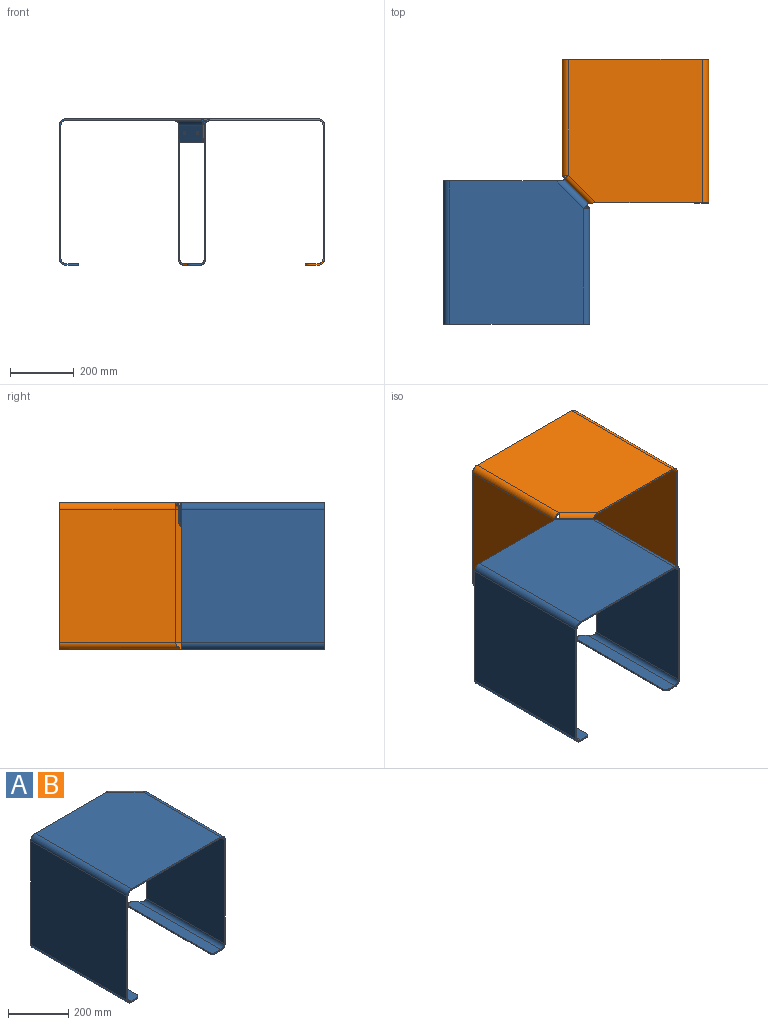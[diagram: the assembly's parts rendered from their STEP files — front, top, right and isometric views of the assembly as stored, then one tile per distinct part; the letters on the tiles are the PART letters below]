
ASSEMBLY  parts=2 mates=1
PART A: 56 faces, bbox 460x464.1x460 mm
  f0: plane 333.93x5mm, normal (0,1,0), area 1669.7mm2, adj f2,f3,f39,f52
  f1: plane 420x5mm, normal (0,-1,0), area 2100mm2, adj f2,f3,f21,f40
  f2: plane 450x420mm, normal (0,0,1), area 185296.3mm2, adj f0,f1,f22,f41,f54
  f3: plane 450x420mm, normal (0,0,-1), area 185296.3mm2, adj f0,f1,f23,f42,f55
  f4: plane 5x1.21mm, normal (0,0,1), area 6.1mm2, adj f6,f7,f8,f20
  f5: plane 420x5mm, normal (0,-1,0), area 2100mm2, adj f7,f8,f17,f21
  f6: plane 420x5mm, normal (0,1,0), area 2100mm2, adj f4,f7,f8,f16
  f7: plane 420x365.15mm, normal (1,0,0), area 153361.8mm2, adj f4,f5,f6,f18,f22
  f8: plane 420x365.15mm, normal (-1,0,0), area 153361.8mm2, adj f4,f5,f6,f19,f23
  f9: plane 25x5mm, normal (0,-1,0), area 125mm2, adj f12,f13,f14,f17
  f10: plane 373.93x5mm, normal (-1,0,0), area 1869.7mm2, adj f12,f13,f14,f15
  f11: plane 14.39x14.39mm, normal (0.71,0.71,0), area 101.8mm2, adj f12,f13,f15,f16
  f12: plane 403.93x40mm, normal (0,0,-1), area 15879.5mm2, adj f9,f10,f11,f14,f15,f18
  f13: plane 403.93x40mm, normal (0,0,1), area 15879.5mm2, adj f9,f10,f11,f14,f15,f19
  f14: cylinder r=15mm len=15mm, axis (0,0,-1), area 117.8mm2, adj f9,f10,f12,f13
  f15: cylinder r=15mm len=25.61mm, axis (0,0,1), area 176.7mm2, adj f10,f11,f12,f13
  f16: bspline ~20x20mm, area 174.7mm2, adj f6,f11,f18,f19
  f17: plane 20x20mm, normal (0,-1,0), area 137.4mm2, adj f5,f9,f18,f19
  f18: cylinder r=20mm len=385.15mm, axis (0,1,0), area 11699.7mm2, adj f7,f12,f16,f17
  f19: cylinder r=15mm len=385.15mm, axis (0,1,0), area 8775.4mm2, adj f8,f13,f16,f17
  f20: plane 20x20mm, normal (0,1,0), area 137.4mm2, adj f4,f22,f23,f53
  f21: plane 20x20mm, normal (0,-1,0), area 137.4mm2, adj f1,f5,f22,f23
  f22: cylinder r=20mm len=363.93mm, axis (0,1,0), area 11433.3mm2, adj f2,f7,f20,f21
  f23: cylinder r=15mm len=363.93mm, axis (0,1,0), area 8575mm2, adj f3,f8,f20,f21
  f24: plane 420x5mm, normal (0,-1,0), area 2100mm2, adj f26,f27,f36,f40
  f25: plane 420x5mm, normal (0,1,0), area 2100mm2, adj f26,f27,f35,f39
  f26: plane 450x420mm, normal (-1,0,0), area 189000mm2, adj f24,f25,f37,f41
  f27: plane 450x420mm, normal (1,0,0), area 189000mm2, adj f24,f25,f38,f42
  f28: plane 420x5mm, normal (1,0,0), area 2100mm2, adj f31,f32,f33,f34
  f29: plane 25x5mm, normal (0,-1,0), area 125mm2, adj f31,f32,f33,f36
  f30: plane 25x5mm, normal (0,1,0), area 125mm2, adj f31,f32,f34,f35
  f31: plane 450x40mm, normal (0,0,-1), area 17903.4mm2, adj f28,f29,f30,f33,f34,f37
  f32: plane 450x40mm, normal (0,0,1), area 17903.4mm2, adj f28,f29,f30,f33,f34,f38
  f33: cylinder r=15mm len=15mm, axis (0,0,-1), area 117.8mm2, adj f28,f29,f31,f32
  f34: cylinder r=15mm len=15mm, axis (0,0,-1), area 117.8mm2, adj f28,f30,f31,f32
  f35: plane 20x20mm, normal (0,1,0), area 137.4mm2, adj f25,f30,f37,f38
  f36: plane 20x20mm, normal (0,-1,0), area 137.4mm2, adj f24,f29,f37,f38
  f37: cylinder r=20mm len=450mm, axis (0,1,0), area 14137.2mm2, adj f26,f31,f35,f36
  f38: cylinder r=15mm len=450mm, axis (0,1,0), area 10602.9mm2, adj f27,f32,f35,f36
  f39: plane 20x20mm, normal (0,1,0), area 137.4mm2, adj f0,f25,f41,f42
  f40: plane 20x20mm, normal (0,-1,0), area 137.4mm2, adj f1,f24,f41,f42
  f41: cylinder r=20mm len=450mm, axis (0,1,0), area 14137.2mm2, adj f2,f26,f39,f40
  f42: cylinder r=15mm len=450mm, axis (0,1,0), area 10602.9mm2, adj f3,f27,f39,f40
  f43: plane 57.78x57.78mm, normal (0,0,-1), area 383.6mm2, adj f48,f49,f50,f51
  f44: plane 40x3.54mm, normal (-0.71,0.71,0), area 200mm2, adj f48,f49,f50,f52
  f45: cylinder r=5.5mm len=11.31mm, axis (0.71,0.71,0), area 172.8mm2, adj f48,f49
  f46: cylinder r=5.5mm len=11.31mm, axis (0.71,0.71,0), area 172.8mm2, adj f48,f49
  f47: plane 40x3.54mm, normal (0.71,-0.71,0), area 200mm2, adj f48,f49,f51,f53
  f48: plane 75.46x75.46mm, normal (0.71,0.71,0), area 5582.7mm2, adj f43,f44,f45,f46,f47,f50,f51,f54
  f49: plane 75.46x75.46mm, normal (-0.71,-0.71,0), area 5582.7mm2, adj f43,f44,f45,f46,f47,f50,f51,f55
  f50: cylinder r=15mm len=15mm, axis (0.71,0.71,0), area 117.8mm2, adj f43,f44,f48,f49
  f51: cylinder r=15mm len=15mm, axis (0.71,0.71,0), area 117.8mm2, adj f43,f47,f48,f49
  f52: bspline ~24.79x20mm, area 161.7mm2, adj f0,f44,f54,f55
  f53: plane 20x14.14mm, normal (0.71,-0.71,0), area 137.4mm2, adj f20,f47,f54,f55
  f54: cylinder r=20mm len=100.21mm, axis (-0.71,0.71,0), area 3508.1mm2, adj f2,f48,f52,f53
  f55: cylinder r=15mm len=96.67mm, axis (-0.71,0.71,0), area 2631.2mm2, adj f3,f49,f52,f53
PART B: same geometry as A
PLACE A t=(185,435,225)mm
PLACE B rot(axis=(0,0,1),180deg) t=(557.82,366.61,225)mm
MATE fastened B.f45 <-> A.f46  axis (-0.71,-0.71,0) through (391.46,380.75,410)mm
